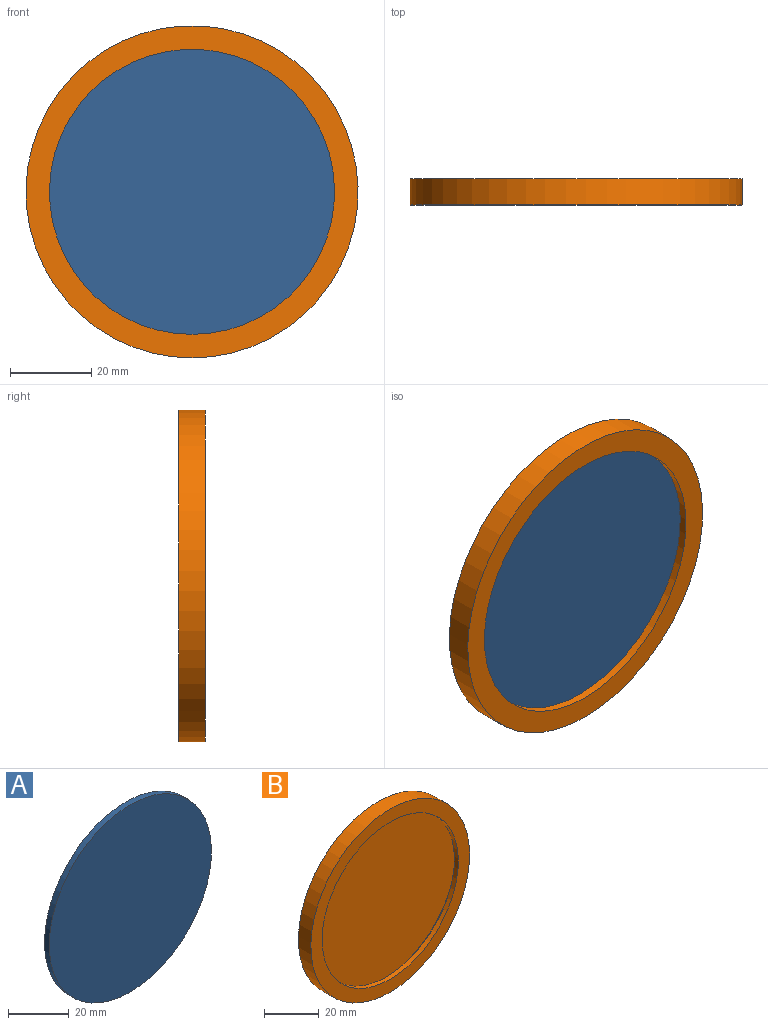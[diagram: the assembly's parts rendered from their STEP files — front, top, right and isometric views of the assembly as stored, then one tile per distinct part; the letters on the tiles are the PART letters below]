
ASSEMBLY  parts=2 mates=1
PART A: 3 faces, bbox 75.8x2.2x75.8 mm
  f0: cylinder r=37.88mm len=75.75mm, axis (0,1,0), area 523.5mm2, adj f1,f2
  f1: plane 75.75x75.75mm, normal (0,-1,0), area 4506.7mm2, adj f0
  f2: plane 75.75x75.75mm, normal (0,1,0), area 4506.7mm2, adj f0
PART B: 7 faces, bbox 81.8x6.4x81.8 mm
  f0: cylinder r=40.88mm len=81.75mm, axis (0,-1,0), area 1643.7mm2, adj f1,f4
  f1: plane 81.75x81.75mm, normal (0,1,0), area 5248.9mm2, adj f0
  f2: plane 76.15x76.15mm, normal (0,1,0), area 689.4mm2, adj f3,f6
  f3: cylinder r=35.08mm len=70.15mm, axis (0,1,0), area 440.8mm2, adj f2,f4
  f4: plane 81.75x81.75mm, normal (0,-1,0), area 1383.9mm2, adj f0,f3
  f5: plane 76.15x76.15mm, normal (0,-1,0), area 4554.4mm2, adj f6
  f6: cylinder r=38.07mm len=76.15mm, axis (0,1,0), area 574.2mm2, adj f2,f5
PLACE A t=(0,-1.1,0)mm
PLACE B at identity
MATE fastened A.f0 <-> B.f0  axis (0,1,0) through (0,0,0)mm
